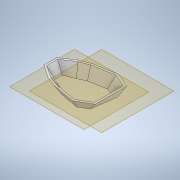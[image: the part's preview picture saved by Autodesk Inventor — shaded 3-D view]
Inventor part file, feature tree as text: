
AUTODESK INVENTOR PART (.ipt)
format: ipt  version: 2022 (Build 260153000, 153)  size: 200,704 bytes
history: native  units: in
note: dims shown in document units (in); Inventor stores cm internally (conversion verified against a paired STEP export)
features: sketch x3, plane x3, loft x1, shell x1
ambient origin geometry x8: Origin, YZ Plane, XZ Plane, XY Plane, X Axis, Y Axis, Z Axis, Center Point
bodies: Body1 (feature_tree)
feature tree (8):
  sketch  "Sketch1"  dims[d2=0.1181in d4=0.962in d5=0.2165in]
  plane  "Work Plane9"
  plane  "Work Plane10"
  plane  "Work Plane15"
  sketch  "Sketch16"  dims[d70=-0.0787in]
  loft  "Loft2"
  shell  "Shell2"  Thickness=0.2165in
  sketch  "Sketch18"  dims[d76=0.1181in d82=0.0984in d86=0.3543in d87=90.0deg d89=0.1969in d90=150.0deg d91=0.2165in d95=0.1969in d97=0.2756in d98=1.1681in d105=0.0591in d106=0.1181in d109=0.0in d110=90.0deg d111=0.0in d112=90.0deg d113=0.0197in d27=0.0197in d28=0.0344in d29=0.0197in d30=0.0344in d34=0.0197in d35=0.0344in d36=0.0197in d37=0.0344in]
